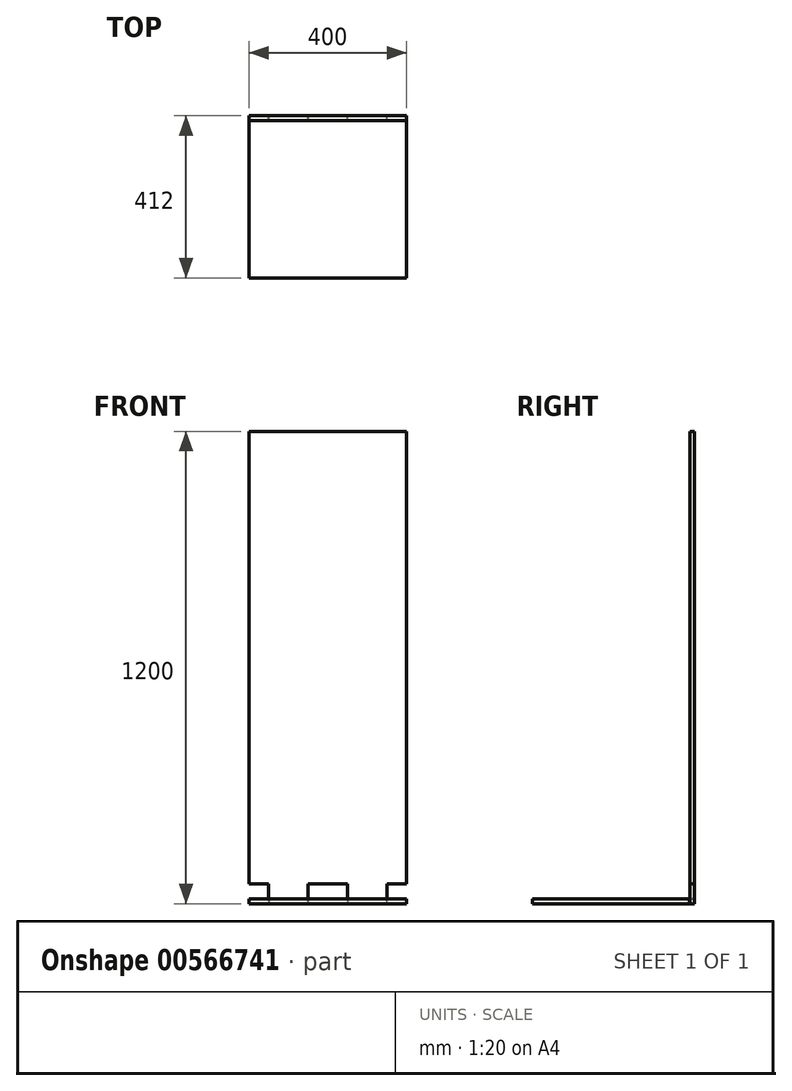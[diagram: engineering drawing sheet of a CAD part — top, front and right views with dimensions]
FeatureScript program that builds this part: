
annotation { "Feature Type Name" : "Feature", "Feature Type Description" : "" }
export const myFeature = defineFeature(function(context is Context, id is Id, definition is map)
    precondition{}
    {
        {
            var Q0;
            Q0=qCreatedBy(makeId("Front.planeOp"),FACE);
            var sketch = newSketch(context, id + "F0", { "sketchPlane" : qUnion([Q0])});
            skLineSegment(sketch, "E0.bottom", {"start": v(50, 0) * mm, "end": v(150, 0) * mm});
            skLineSegment(sketch, "E0.top", {"start": v(0, 1200) * mm, "end": v(400, 1200) * mm});
            skLineSegment(sketch, "E0.left", {"start": v(0, 50) * mm, "end": v(0, 1200) * mm});
            skLineSegment(sketch, "E0.right", {"start": v(400, 50) * mm, "end": v(400, 1200) * mm});
            skLineSegment(sketch, "E1", {"start": v(0, 50) * mm, "end": v(50, 50) * mm});
            skLineSegment(sketch, "E2", {"start": v(50, 50) * mm, "end": v(50, 0) * mm});
            skLineSegment(sketch, "E3", {"start": v(150, 0) * mm, "end": v(150, 50) * mm});
            skLineSegment(sketch, "E4", {"start": v(150, 50) * mm, "end": v(250, 50) * mm});
            skLineSegment(sketch, "E5", {"start": v(250, 50) * mm, "end": v(250, 0) * mm});
            skLineSegment(sketch, "E6", {"start": v(350, 0) * mm, "end": v(350, 50) * mm});
            skLineSegment(sketch, "E7", {"start": v(350, 50) * mm, "end": v(400, 50) * mm});
            skLineSegment(sketch, "E8.trimOffspring", {"start": v(250, 0) * mm, "end": v(350, 0) * mm});
            skSolve(sketch);
        }
        {
            var Q0;
            Q0 = qSketchRegion(id + "F0", true);
            extrude(context, id + "F1", {"entities" : qUnion([Q0]), "depth" : 12 * mm, "offsetDistance" : 25 * mm});
        }
        {
            var Q0;
            Q0=qCreatedBy(makeId("Top.planeOp"),FACE);
            var sketch = newSketch(context, id + "F2", { "sketchPlane" : qUnion([Q0])});
            skLineSegment(sketch, "E9", {"start": v(0, -12.5) * mm, "end": v(50.5, -12.5) * mm});
            skLineSegment(sketch, "E10", {"start": v(50.5, -12.5) * mm, "end": v(50.5, 0) * mm});
            skLineSegment(sketch, "E11", {"start": v(50.5, 0) * mm, "end": v(149.5, 0) * mm});
            skLineSegment(sketch, "E12", {"start": v(149.5, 0) * mm, "end": v(149.5, -12.5) * mm});
            skLineSegment(sketch, "E13", {"start": v(149.5, -12.5) * mm, "end": v(250.5, -12.5) * mm});
            skLineSegment(sketch, "E14", {"start": v(250.5, -12.5) * mm, "end": v(250.5, 0) * mm});
            skLineSegment(sketch, "E15", {"start": v(250.5, 0) * mm, "end": v(349.5, 0) * mm});
            skLineSegment(sketch, "E16", {"start": v(349.5, 0) * mm, "end": v(349.5, -12.5) * mm});
            skLineSegment(sketch, "E17", {"start": v(349.5, -12.5) * mm, "end": v(399.5, -12.5) * mm});
            skLineSegment(sketch, "E18", {"start": v(399.5, -12.5) * mm, "end": v(399.5, -412) * mm});
            skLineSegment(sketch, "E19", {"start": v(399.5, -412) * mm, "end": v(0, -412) * mm});
            skLineSegment(sketch, "E20", {"start": v(0, -412) * mm, "end": v(0, -12.5) * mm});
            skSolve(sketch);
        }
        {
            var Q0;
            Q0=makeQuery(id+"F2.imprint","IMPRINT",FACE,{"disambiguationData":[TD([[makeQuery(id+"F2.imprint","IMPRINT",EDGE,{"derivedFrom":sQuery(id+"F2.wireOp",EDGE,"E9")}),-1.0]])]});
            var Q1;
            Q1=sQuery(id+"F2.wireOp",EDGE,"E20");
            extrude(context, id + "F3", {"entities" : qUnion([Q0]), "surfaceEntities" : qUnion([Q1]), "depth" : 12 * mm, "offsetDistance" : 25 * mm});
        }
    });
